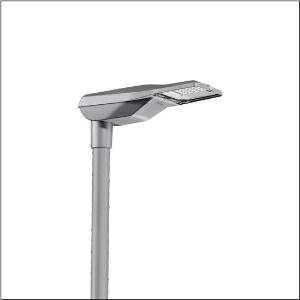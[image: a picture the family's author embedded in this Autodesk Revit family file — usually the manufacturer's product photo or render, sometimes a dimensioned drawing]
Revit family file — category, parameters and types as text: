
# Revit family: streetlight_sl_21_iq_micro___stw1_0a_5xe1e21d08cb_e74e
name_source: partatom
category: Lighting Fixtures
units: mm (PartAtom-declared; Revit-internal decimal feet)

## family parameters
Cut with Voids When Loaded = No
Host = Face
Light Source = No
Part Type = Normal
Room Calculation Point = No
Round Connector Dimension = Use Diameter
Shared = No

## types (1)
- --- (1 x LED, 2380 lm, 19.4 W, 2200K)
    Apparent Load = 19 VA
    CIE Flux Codes = 38 75 98 100 100
    Color Rendering = 70
    Color Temperature = 2200K
    Default Elevation = 1800 mm
    Description = Streetlight SL 21 iQ micro, mast luminaire, primary light control with lens, of PMMA, primary optical cover: cover, of toughened safety glass, transparent, light distribution: STW1.0a, light emission: direct distribution, primary light characteristic: asymmetric, installation type: post-top, side-entry, LED, High Power LED, rated luminous flux: 2.380lm, luminous efficacy: 123lm/W, light colour: 722, colour temperature: 2200K, control: Auto-Match, Temp-Guard, Lumen-Switch, Night-Set, Smart-Wire, Light-Fading, Desk-Remote (wireless, voltage-free reading and setting of iQ features in the workshop via application-optimized NFC function/RFID function), optimised constant luminous flux control (CLO 2.0), pre-setting: linear dimming characteristic, mains connection: 220..240V, AC, 50/60Hz, start of lifetime: 19W, end of service life: 20W, reduction: 10W, luminaire housing, of diecast aluminium, powder-coated, Siteco® metallic grey (DB 702S), corrosivity category C5 mid according to DIN EN ISO 12944, please order mast flange separately, inclination adjustable: 0°, 5°, 10°, 15°, sealing non-destructively replaceable, multi-level sealing system, length: 528mm, width: 235mm, height: 110mm, mast flange for spigot size: 42mm (side-entry): 5XC10008XM4, 60/48mm (side-entry/post-top): 5XC10108XM2, 76/60mm (side-entry/post-top): 5XC10108XM1, protection rating (complete): IP66, insulation class (complete): insulation class II (safety insulation), certification: CE, ENEC, ENEC+, VDE, impact resistance: IK09, permissible operating ambient temperature for outdoor applications: -40..+50°C, standard-compliant lighting for roads and squares, packaging unit: 1 piece

Light Distribution: STW1.0a
    Height = 110 mm
    Lamp = 1 x LED
    Lamp Light Flux = 2380 lm
    Lamp Power = 19.4 W
    Lamp count = 1
    Length = 528 mm
    Luminous efficacy = 123 lm/W
    Manufacturer = Siteco
    ModVariant = No
    Model = 5XE1E21D08CB
    Number of Poles = 1
    OnlyDefault = Yes
    Power Factor = 1
    Product Name = Streetlight SL 21 iQ micro | STW1.0a
    Product group = mast luminaire | pylon top
    ProductGroupID = 6100
    Protection Class = Protection class II
    Protection Degree = IP 66
    RLX_Detail_Level = 1
    RLX_Emergency_Light_Flux = 0 lm
    RLX_Emergency_Type = 0
    RLX_Emergency_Type_DB = No
    RlxData = <blob elided: 98397 chars, md5=8dc0b9dc>
    Socket = socket
    Standby Power = 0 W
    System Light Flux = 2380 lm
    System Power = 19 W
    Type Comments = factory setting: luminous flux: 100 % | dim-lin: 254 | 387 mA
    Type Image = l_1006881.jpg
    URL = http://relux.com
    VarID = @adj_108771
    Voltage = 0 V
    Weight = 0.00 kg
    Width = 235 mm

## geometry (parser evidence)
native form markers: Blend x4, Sweep x10
no freeform markers — native parametric forms only
